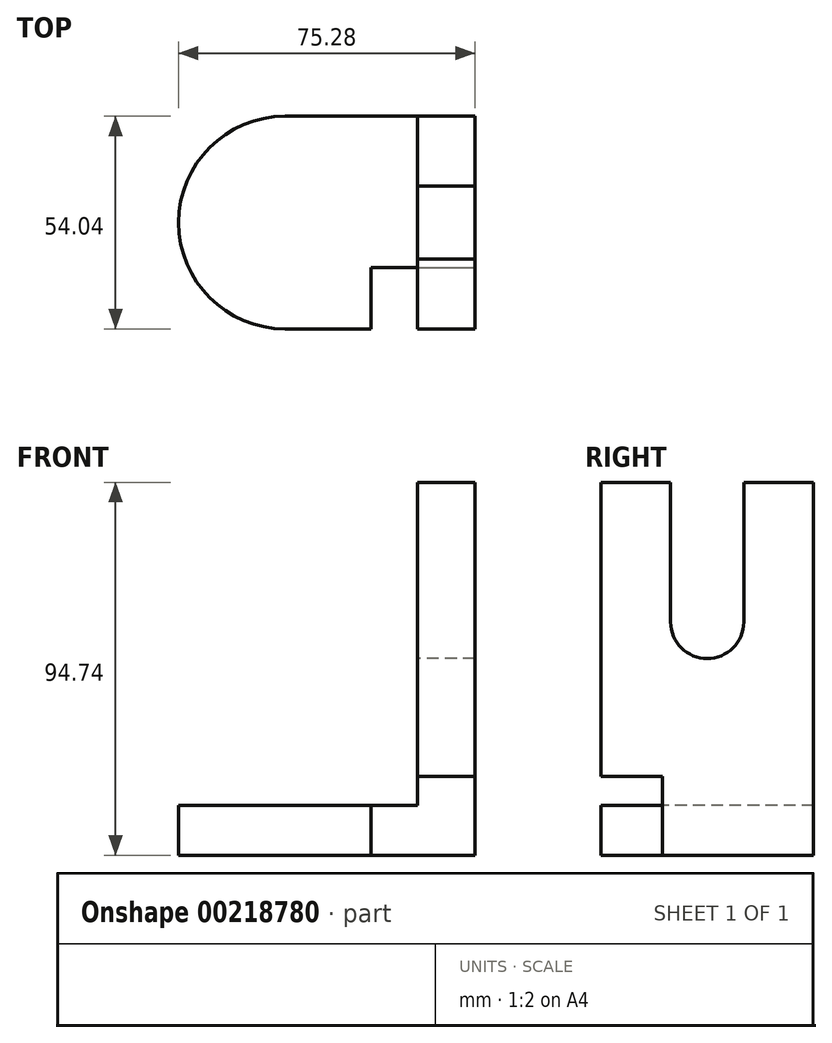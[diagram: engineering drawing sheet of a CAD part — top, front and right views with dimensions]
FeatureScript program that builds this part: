
annotation { "Feature Type Name" : "Feature", "Feature Type Description" : "" }
export const myFeature = defineFeature(function(context is Context, id is Id, definition is map)
    precondition{}
    {
        {
            var Q0;
            Q0=qCreatedBy(makeId("Top.planeOp"),FACE);
            var sketch = newSketch(context, id + "F0", { "sketchPlane" : qUnion([Q0])});
            skArc(sketch, "E0", {"start": v(-48.26, 27.02) * mm, "mid": v(-75.28, 0) * mm, "end": v(-48.26, -27.02) * mm});
            skLineSegment(sketch, "E1", {"start": v(-48.26, 27.02) * mm, "end": v(0, 27.02) * mm});
            skLineSegment(sketch, "E2", {"start": v(-48.26, -27.02) * mm, "end": v(0, -27.02) * mm});
            skLineSegment(sketch, "E3", {"start": v(0, -27.02) * mm, "end": v(0, 27.02) * mm});
            skSolve(sketch);
        }
        {
            var Q0;
            Q0=makeQuery(id+"F0.imprint","IMPRINT",FACE,{"disambiguationData":[TD([[makeQuery(id+"F0.imprint","IMPRINT",EDGE,{"derivedFrom":sQuery(id+"F0.wireOp",EDGE,"E0")}),1.0]])]});
            extrude(context, id + "F1", {"entities" : qUnion([Q0]), "depth" : 12.7 * mm});
        }
        {
            var Q0;
            Q0=makeQuery(id+"F1.opExtrude","CAP_FACE",FACE,{"disambiguationData":[OSD([sQuery(id+"F0.wireOp",EDGE,"E0"),sQuery(id+"F0.wireOp",EDGE,"E1"),sQuery(id+"F0.wireOp",EDGE,"E2"),sQuery(id+"F0.wireOp",EDGE,"E3")])],"isStart":false});
            var sketch = newSketch(context, id + "F2", { "sketchPlane" : qUnion([Q0])});
            skLineSegment(sketch, "E4.bottom", {"start": v(0, 27.02) * mm, "end": v(-14.55, 27.02) * mm});
            skLineSegment(sketch, "E4.top", {"start": v(0, -27.02) * mm, "end": v(-14.55, -27.02) * mm});
            skLineSegment(sketch, "E4.left", {"start": v(0, 27.02) * mm, "end": v(0, -27.02) * mm});
            skLineSegment(sketch, "E4.right", {"start": v(-14.55, 27.02) * mm, "end": v(-14.55, -27.02) * mm});
            skSolve(sketch);
        }
        {
            var Q0;
            Q0=makeQuery(id+"F2.imprint","IMPRINT",FACE,{"disambiguationData":[TD([[makeQuery(id+"F2.imprint","IMPRINT",EDGE,{"derivedFrom":sQuery(id+"F2.wireOp",EDGE,"E4.bottom")}),-1.0]])]});
            extrude(context, id + "F3", {"entities" : qUnion([Q0]), "operationType" : NewBodyOperationType.ADD, "depth" : 82.04 * mm});
        }
        {
            var Q0;
            Q0=makeQuery(id+"F3.opExtrude","SWEPT_FACE",FACE,{"disambiguationData":[OSD([sQuery(id+"F2.wireOp",EDGE,"E4.right")])]});
            var sketch = newSketch(context, id + "F4", { "sketchPlane" : qUnion([Q0])});
            skArc(sketch, "E5", {"start": v(-9.3, 59.27) * mm, "mid": v(0, 49.98) * mm, "end": v(9.3, 59.27) * mm});
            skLineSegment(sketch, "E6", {"start": v(-9.3, 59.27) * mm, "end": v(-9.3, 94.74) * mm});
            skLineSegment(sketch, "E7", {"start": v(9.3, 59.27) * mm, "end": v(9.3, 94.74) * mm});
            skLineSegment(sketch, "E8", {"start": v(9.3, 94.74) * mm, "end": v(-9.3, 94.74) * mm});
            skSolve(sketch);
        }
        {
            var Q0;
            Q0=makeQuery(id+"F4.imprint","IMPRINT",FACE,{"disambiguationData":[TD([[makeQuery(id+"F4.imprint","IMPRINT",EDGE,{"derivedFrom":sQuery(id+"F4.wireOp",EDGE,"E5")}),1.0]])]});
            extrude(context, id + "F5", {"entities" : qUnion([Q0]), "operationType" : NewBodyOperationType.REMOVE, "oppositeDirection" : true, "depth" : 25.4 * mm});
        }
        {
            var Q0;
            Q0=makeQuery(id+"F3.boolean.opBoolean","MERGE",FACE,{"derivedFrom":[makeQuery(id+"F1.opExtrude","SWEPT_FACE",FACE,{"disambiguationData":[OSD([sQuery(id+"F0.wireOp",EDGE,"E3")])]}),makeQuery(id+"F3.opExtrude","SWEPT_FACE",FACE,{"disambiguationData":[OSD([sQuery(id+"F2.wireOp",EDGE,"E4.left")])]})]});
            var sketch = newSketch(context, id + "F6", { "sketchPlane" : qUnion([Q0])});
            skLineSegment(sketch, "E9.bottom", {"start": v(-27.02, 0) * mm, "end": v(-11.37, 0) * mm});
            skLineSegment(sketch, "E9.top", {"start": v(-27.02, 20.01) * mm, "end": v(-11.37, 20.01) * mm});
            skLineSegment(sketch, "E9.left", {"start": v(-27.02, 0) * mm, "end": v(-27.02, 20.01) * mm});
            skLineSegment(sketch, "E9.right", {"start": v(-11.37, 0) * mm, "end": v(-11.37, 20.01) * mm});
            skSolve(sketch);
        }
        {
            var Q0;
            Q0=makeQuery(id+"F6.imprint","IMPRINT",FACE,{"disambiguationData":[TD([[makeQuery(id+"F6.imprint","IMPRINT",EDGE,{"derivedFrom":sQuery(id+"F6.wireOp",EDGE,"E9.bottom")}),1.0]])]});
            extrude(context, id + "F7", {"entities" : qUnion([Q0]), "operationType" : NewBodyOperationType.REMOVE, "oppositeDirection" : true, "depth" : 26.42 * mm});
        }
    });
